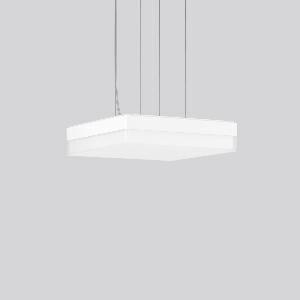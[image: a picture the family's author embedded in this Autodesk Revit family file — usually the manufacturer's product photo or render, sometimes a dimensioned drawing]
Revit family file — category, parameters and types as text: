
# Revit family: flat_slim_square_312541_002_bf27
name_source: partatom
category: Lighting Fixtures
units: mm (PartAtom-declared; Revit-internal decimal feet)

## family parameters
Cut with Voids When Loaded = No
Host = Face
Light Source = No
Part Type = Normal
Room Calculation Point = No
Round Connector Dimension = Use Diameter
Shared = No

## types (1)
- MultiLumen 2 840 (1 x LED Modul 840, 2300 lm, 4000)
    Apparent Load = 19 VA
    CIE Flux Codes = 43 74 93 92 100
    Color Rendering = 80
    Color Temperature = 4000
    Default Elevation = 1800 mm
    Height = 70 mm
    Lamp = 1 x LED Modul 840
    Lamp Light Flux = 2300 lm
    Lamp count = 1
    Length = 300 mm
    Lifetime = 50000 h
    Luminous efficacy = 121 lm/W
    Manufacturer = RZB
    ModVariant = No
    Model = 312541.002
    Mounting Place = Ceiling
    Mounting Type = Pendant
    Number of Poles = 1
    OnlyDefault = Yes
    Power Factor = 1
    Product Name = FLAT SLIM square
    Product group = Pendant luminaires
    ProductGroupID = 902
    Protection Class = Protection class I
    Protection Degree = IP 40
    RLX_Detail_Level = 1
    RLX_Emergency_Light_Flux = 0 lm
    RLX_Emergency_Type = 0
    RLX_Emergency_Type_DB = No
    RlxData = <blob elided: 14213 chars, md5=9d732b0d>
    Socket = socket
    Standby Power = 0 W
    System Light Flux = 2300 lm
    System Power = 19 W
    Type Comments = MultiLumen 2 840
    Type Image = 312541.002.jpg
    URL = http://relux.com
    VarID = multilumen_2_840
    Voltage = 230 V
    Voltage Range = 220-240 V
    Weight = 0.00 kg
    Width = 300 mm

## geometry (parser evidence)
native form markers: Sweep x15
no freeform markers — native parametric forms only
